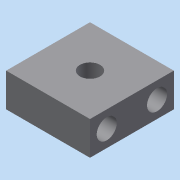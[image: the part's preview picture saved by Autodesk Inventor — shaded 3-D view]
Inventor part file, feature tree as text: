
AUTODESK INVENTOR PART (.ipt)
format: ipt  version: 2015 (Build 190159000, 159)  size: 94,208 bytes
history: native  units: in
note: dims shown in document units (in); Inventor stores cm internally (conversion verified against a paired STEP export)
features: sketch x3, hole x2, extrude x1
ambient origin geometry x8: Origin, YZ Plane, XZ Plane, XY Plane, X Axis, Y Axis, Z Axis, Center Point
bodies: Solid1 (feature_tree)
feature tree (6):
  extrude  "Extrusion1"  Depth=1.9685in
  hole  "Hole1"  [1 undecoded]
  hole  "Hole2"  [1 undecoded]
  sketch  "Sketch1"  dims[d0=1.9685in d1=1.9685in]
  sketch  "Sketch2"  dims[d2=0.7874in d3=0.0in d4=0.3937in]
  sketch  "Sketch3"  dims[d5=0.3937in d6=0.3937in d7=0.3937in d8=0.4724in d9=0.2362in d10=0.1575in d11=0.0787in d12=90.0deg d13=1.9685in d14=0.8108in d15=0.9843in d16=0.9843in d17=0.4724in d18=0.2362in d19=0.1575in d20=0.0787in d21=90.0deg d22=1.9685in d23=0.8108in]
note: 2 required parameter values undecoded (feature->parameter linkage not recoverable at this tier; creation-order binding heuristic only, values carry confidence <= 0.55)
